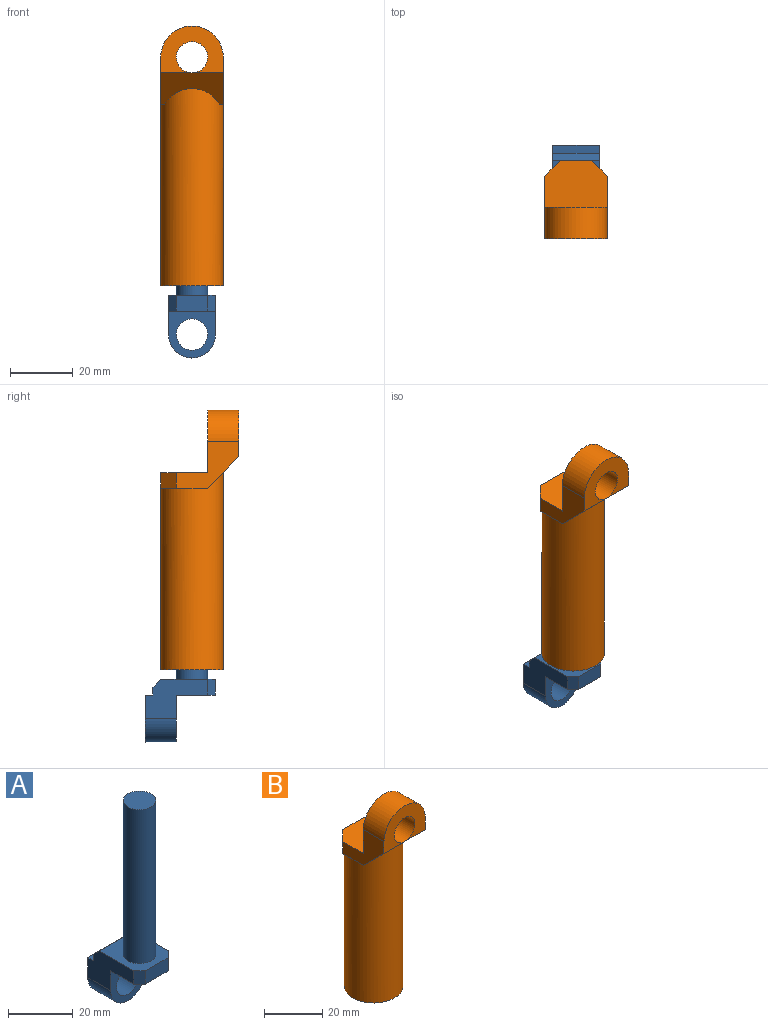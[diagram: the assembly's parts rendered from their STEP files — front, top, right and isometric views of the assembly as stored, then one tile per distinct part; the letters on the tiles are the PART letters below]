
ASSEMBLY  parts=2 mates=1
PART A: 16 faces, bbox 15x22.5x78.1 mm
  f0: plane 20x12.5mm, normal (1,0,0), area 159.4mm2, adj f4,f5,f8,f9,f10,f11,f12,f13
  f1: cylinder r=5mm len=10mm, axis (0,-1,0), area 314.2mm2, adj f11,f12
  f2: plane 10x10mm, normal (0,0,1), area 78.5mm2, adj f3
  f3: cylinder r=5mm len=58.08mm, axis (0,0,1), area 1824.5mm2, adj f2,f5
  f4: plane 15x12.5mm, normal (0,0,-1), area 181.3mm2, adj f0,f6,f7,f12,f14,f15
  f5: plane 17.5x15mm, normal (0,0,1), area 177.7mm2, adj f0,f3,f6,f7,f13,f14,f15
  f6: plane 20x12.5mm, normal (-1,0,0), area 159.4mm2, adj f4,f5,f8,f9,f10,f11,f12,f13
  f7: plane 10x5mm, normal (0,-1,0), area 50mm2, adj f4,f5,f14,f15
  f8: plane 15x2.5mm, normal (0,1,0), area 37.5mm2, adj f0,f6,f9,f13
  f9: plane 15x2.5mm, normal (0,0,1), area 37.5mm2, adj f0,f6,f8,f11
  f10: cylinder r=7.5mm len=15mm, axis (0,-1,0), area 235.6mm2, adj f0,f6,f11,f12
  f11: plane 15x15mm, normal (0,1,0), area 122.3mm2, adj f0,f1,f6,f9,f10
  f12: plane 15x15mm, normal (0,-1,0), area 122.3mm2, adj f0,f1,f4,f6,f10
  f13: plane 15x2.5mm, normal (0,0.71,0.71), area 53mm2, adj f0,f5,f6,f8
  f14: plane 5x2.5mm, normal (0.71,-0.71,0), area 17.7mm2, adj f0,f4,f5,f7
  f15: plane 5x2.5mm, normal (-0.71,-0.71,0), area 17.7mm2, adj f4,f5,f6,f7
PART B: 19 faces, bbox 20x25x83.1 mm
  f0: plane 20x15mm, normal (1,0,0), area 150mm2, adj f1,f6,f9,f12,f14,f15,f16,f17
  f1: plane 20x15mm, normal (0,0,1), area 275mm2, adj f0,f10,f11,f15,f17,f18
  f2: cylinder r=10mm len=63.09mm, axis (0,0,1), area 3717.6mm2, adj f4,f6,f7,f8,f9,f16
  f3: cylinder r=5mm len=58.08mm, axis (0,0,1), area 1824.5mm2, adj f4,f5
  f4: plane 20x20mm, normal (0,0,-1), area 235.6mm2, adj f2,f3
  f5: plane 10x10mm, normal (0,0,-1), area 78.5mm2, adj f3
  f6: plane 10x10mm, normal (0,0,-1), area 9mm2, adj f0,f2,f11,f17
  f7: plane 10x10mm, normal (0,0,-1), area 9mm2, adj f2,f10,f11,f18
  f8: plane 5x1.34mm, normal (0,0,-1), area 2.2mm2, adj f2,f10,f16
  f9: plane 5x1.34mm, normal (0,0,-1), area 2.2mm2, adj f0,f2,f16
  f10: plane 20x15mm, normal (-1,0,0), area 150mm2, adj f1,f7,f8,f12,f14,f15,f16,f18
  f11: plane 10x5mm, normal (0,1,0), area 50mm2, adj f1,f6,f7,f17,f18
  f12: cylinder r=10mm len=20mm, axis (0,1,0), area 314.2mm2, adj f0,f10,f14,f15
  f13: cylinder r=5mm len=10mm, axis (0,1,0), area 314.2mm2, adj f14,f15
  f14: plane 20x15mm, normal (0,-1,0), area 178.5mm2, adj f0,f10,f12,f13,f16
  f15: plane 20x20mm, normal (0,1,0), area 278.5mm2, adj f0,f1,f10,f12,f13
  f16: plane 20x10mm, normal (0,-0.71,-0.71), area 196mm2, adj f0,f2,f8,f9,f10,f14
  f17: plane 5x5mm, normal (0.71,0.71,0), area 35.4mm2, adj f0,f1,f6,f11
  f18: plane 5x5mm, normal (-0.71,0.71,0), area 35.4mm2, adj f1,f7,f10,f11
PLACE A t=(29.2,24.22,80.89)mm
PLACE B rot(axis=(-0.09,0.99,-0.04),0deg) t=(29.2,24.22,30.89)mm
MATE slider A.f3 <-> B.f2  axis (0,0,1) through (83.29,24.22,38.78)mm
